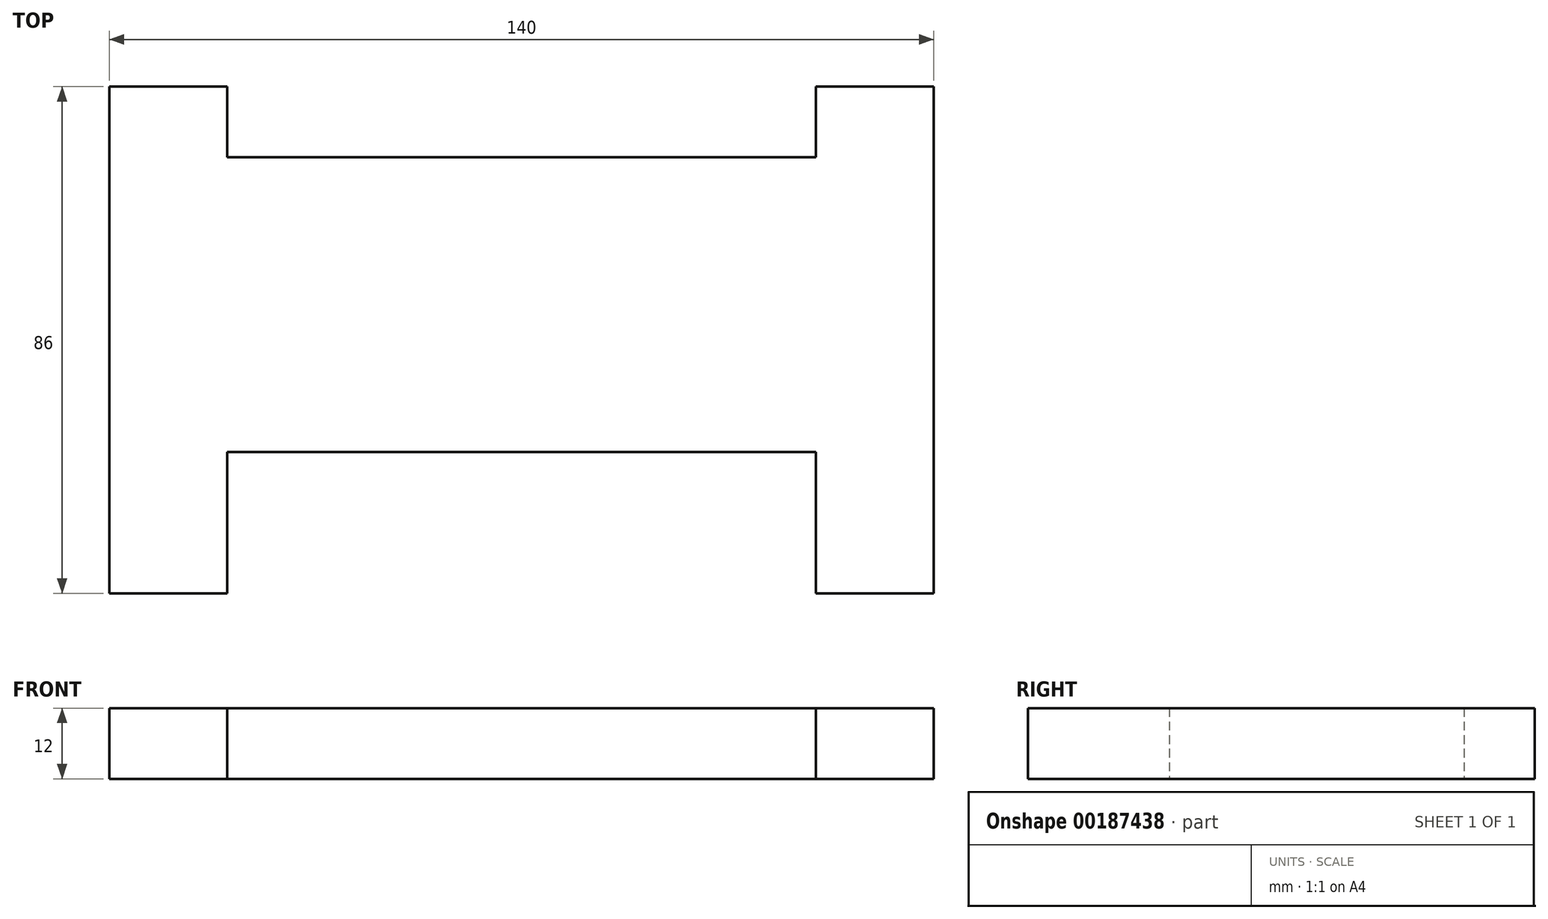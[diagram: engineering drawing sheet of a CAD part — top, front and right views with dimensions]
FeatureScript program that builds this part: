
annotation { "Feature Type Name" : "Feature", "Feature Type Description" : "" }
export const myFeature = defineFeature(function(context is Context, id is Id, definition is map)
    precondition{}
    {
        {
            var Q0;
            Q0=qCreatedBy(makeId("Top.planeOp"),FACE);
            var sketch = newSketch(context, id + "F0", { "sketchPlane" : qUnion([Q0])});
            skLineSegment(sketch, "E0.bottom", {"start": v(70, 25) * mm, "end": v(-70, 25) * mm});
            skLineSegment(sketch, "E0.top", {"start": v(70, -25) * mm, "end": v(-70, -25) * mm});
            skLineSegment(sketch, "E0.left", {"start": v(70, 25) * mm, "end": v(70, -25) * mm});
            skLineSegment(sketch, "E0.right", {"start": v(-70, 25) * mm, "end": v(-70, -25) * mm});
            skPoint(sketch, "E0.middle", {"position": v(0, 0) * mm});
            skLineSegment(sketch, "E1.bottom", {"start": v(-70, -25) * mm, "end": v(-50, -25) * mm});
            skLineSegment(sketch, "E1.top", {"start": v(-70, -37) * mm, "end": v(-50, -37) * mm});
            skLineSegment(sketch, "E1.left", {"start": v(-70, -25) * mm, "end": v(-70, -37) * mm});
            skLineSegment(sketch, "E1.right", {"start": v(-50, -25) * mm, "end": v(-50, -37) * mm});
            skLineSegment(sketch, "E2.MirrorCS", {"start": v(50, -25) * mm, "end": v(50, -37) * mm});
            skLineSegment(sketch, "E3.MirrorCS", {"start": v(70, -25) * mm, "end": v(70, -37) * mm});
            skLineSegment(sketch, "E4.MirrorCS", {"start": v(70, -25) * mm, "end": v(50, -25) * mm});
            skLineSegment(sketch, "E5.MirrorCS", {"start": v(70, -37) * mm, "end": v(50, -37) * mm});
            skLineSegment(sketch, "E6.MirrorCS", {"start": v(70, 37) * mm, "end": v(50, 37) * mm});
            skLineSegment(sketch, "E7.MirrorCS", {"start": v(70, 25) * mm, "end": v(50, 25) * mm});
            skLineSegment(sketch, "E8.MirrorCS", {"start": v(70, 25) * mm, "end": v(70, 37) * mm});
            skLineSegment(sketch, "E9.MirrorCS", {"start": v(-70, 25) * mm, "end": v(-50, 25) * mm});
            skLineSegment(sketch, "E10.MirrorCS", {"start": v(50, 25) * mm, "end": v(50, 37) * mm});
            skLineSegment(sketch, "E11.MirrorCS", {"start": v(-50, 25) * mm, "end": v(-50, 37) * mm});
            skLineSegment(sketch, "E12.MirrorCS", {"start": v(-70, 25) * mm, "end": v(-70, 37) * mm});
            skLineSegment(sketch, "E13.MirrorCS", {"start": v(-70, 37) * mm, "end": v(-50, 37) * mm});
            skSolve(sketch);
        }
        {
            var Q0;
            Q0 = qSketchRegion(id + "F0", true);
            extrude(context, id + "F1", {"entities" : qUnion([Q0]), "depth" : 12 * mm, "offsetDistance" : 25 * mm});
        }
        {
            var Q0;
            Q0=makeQuery(id+"F1.opExtrude","SWEPT_FACE",FACE,{"disambiguationData":[OSD([sQuery(id+"F0.wireOp",EDGE,"E1.top")])]});
            var Q1;
            Q1=makeQuery(id+"F1.opExtrude","SWEPT_FACE",FACE,{"disambiguationData":[OSD([sQuery(id+"F0.wireOp",EDGE,"E5.MirrorCS")])]});
            extrude(context, id + "F2", {"entities" : qUnion([Q0, Q1]), "operationType" : NewBodyOperationType.ADD, "depth" : 12 * mm, "offsetDistance" : 25 * mm});
        }
    });
